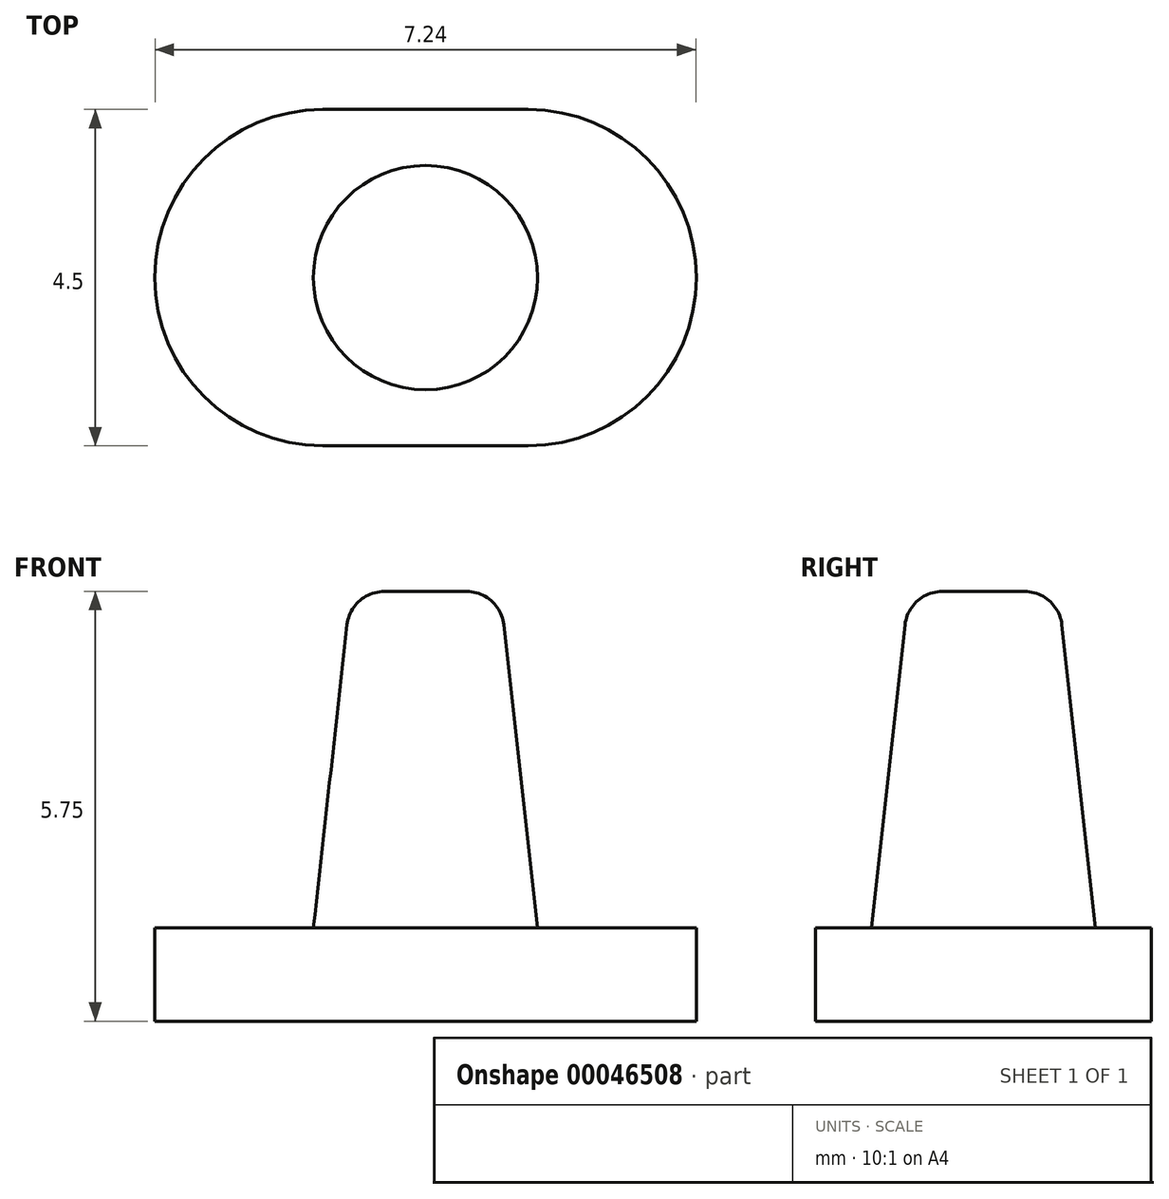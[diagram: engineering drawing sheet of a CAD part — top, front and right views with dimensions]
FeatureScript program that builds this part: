
annotation { "Feature Type Name" : "Feature", "Feature Type Description" : "" }
export const myFeature = defineFeature(function(context is Context, id is Id, definition is map)
    precondition{}
    {
        {
            var Q0;
            Q0=qCreatedBy(makeId("Top.planeOp"),FACE);
            var sketch = newSketch(context, id + "F0", { "sketchPlane" : qUnion([Q0])});
            skLineSegment(sketch, "E0.rect.bottom", {"start": v(-3.62, 2.25) * mm, "end": v(3.62, 2.25) * mm, "construction": true});
            skLineSegment(sketch, "E0.rect.top", {"start": v(-3.62, -2.25) * mm, "end": v(3.62, -2.25) * mm, "construction": true});
            skLineSegment(sketch, "E0.rect.left", {"start": v(-3.63, 2.25) * mm, "end": v(-3.63, -2.25) * mm, "construction": true});
            skLineSegment(sketch, "E0.rect.right", {"start": v(3.62, 2.25) * mm, "end": v(3.62, -2.25) * mm, "construction": true});
            skPoint(sketch, "E0.rect.middle", {"position": v(0, 0) * mm});
            skArc(sketch, "E1", {"start": v(1.38, -2.25) * mm, "mid": v(3.62, 0) * mm, "end": v(1.37, 2.25) * mm});
            skLineSegment(sketch, "E2", {"start": v(1.37, 2.25) * mm, "end": v(1.37, 0) * mm, "construction": true});
            skLineSegment(sketch, "E3", {"start": v(1.37, 0) * mm, "end": v(1.38, -2.25) * mm, "construction": true});
            skArc(sketch, "E4", {"start": v(-1.38, 2.25) * mm, "mid": v(-3.63, 0) * mm, "end": v(-1.38, -2.25) * mm});
            skLineSegment(sketch, "E5", {"start": v(-1.38, 2.25) * mm, "end": v(-1.38, 0) * mm, "construction": true});
            skLineSegment(sketch, "E6", {"start": v(-1.38, 0) * mm, "end": v(-1.38, -2.25) * mm, "construction": true});
            skLineSegment(sketch, "E7", {"start": v(-1.38, 2.25) * mm, "end": v(1.37, 2.25) * mm});
            skLineSegment(sketch, "E8", {"start": v(-1.38, -2.25) * mm, "end": v(1.38, -2.25) * mm});
            skSolve(sketch);
        }
        {
            var Q0;
            Q0 = qSketchRegion(id + "F0", true);
            extrude(context, id + "F1", {"entities" : qUnion([Q0]), "depth" : 1.25 * mm});
        }
        {
            var Q0;
            Q0=qCreatedBy(makeId("Front.planeOp"),FACE);
            var sketch = newSketch(context, id + "F2", { "sketchPlane" : qUnion([Q0])});
            skLineSegment(sketch, "E9.0", {"start": v(-1.38, 1.25) * mm, "end": v(1.38, 1.25) * mm, "construction": true});
            skLineSegment(sketch, "E10", {"start": v(0, 1.25) * mm, "end": v(0, 5.75) * mm});
            skPoint(sketch, "E10.endSnap0", {"position": v(0, 1.25) * mm});
            skLineSegment(sketch, "E11", {"start": v(0, 5.75) * mm, "end": v(-0.55, 5.75) * mm});
            skLineSegment(sketch, "E12", {"start": v(-1.05, 5.3) * mm, "end": v(-1.5, 1.25) * mm});
            skLineSegment(sketch, "E13", {"start": v(-1.5, 1.25) * mm, "end": v(0, 1.25) * mm});
            skPoint(sketch, "E14.visualSharp", {"position": v(-1, 5.75) * mm});
            skArc(sketch, "E14.filletArc", {"start": v(-0.55, 5.75) * mm, "mid": v(-0.89, 5.62) * mm, "end": v(-1.05, 5.3) * mm});
            skSolve(sketch);
        }
        {
            var Q0;
            Q0 = qSketchRegion(id + "F2", true);
            var Q1;
            Q1=sQuery(id+"F2.wireOp",EDGE,"E10");
            revolve(context, id + "F3", {"operationType" : NewBodyOperationType.ADD, "entities" : qUnion([Q0]), "axis" : qUnion([Q1]), "revolveType" : RevolveType.FULL});
        }
    });
